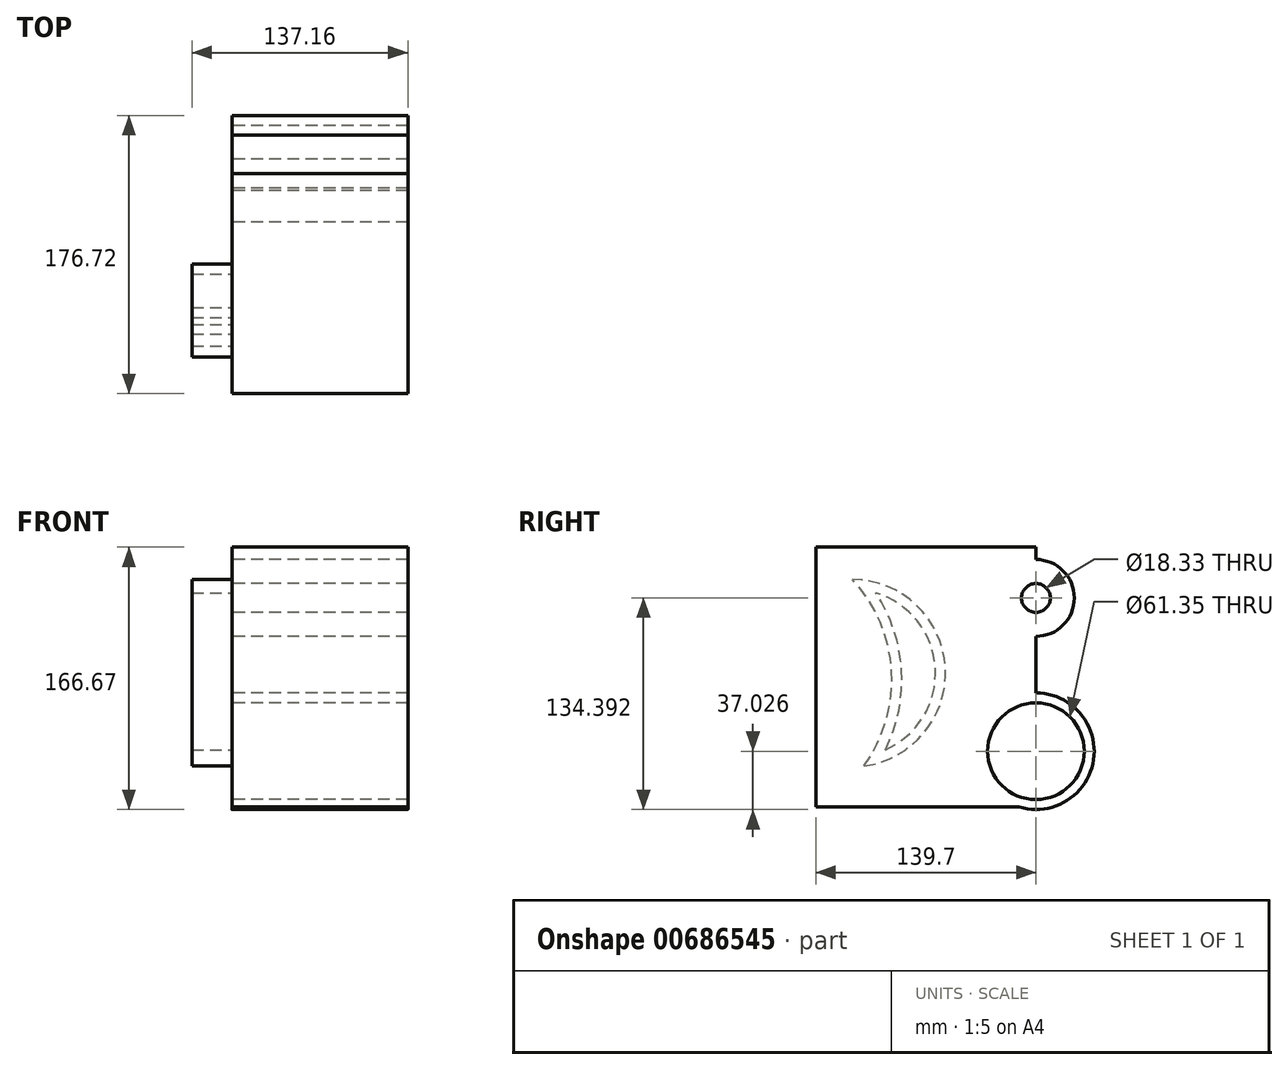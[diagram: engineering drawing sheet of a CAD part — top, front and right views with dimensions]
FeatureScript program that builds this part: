
annotation { "Feature Type Name" : "Feature", "Feature Type Description" : "" }
export const myFeature = defineFeature(function(context is Context, id is Id, definition is map)
    precondition{}
    {
        {
            var Q0;
            Q0=qCreatedBy(makeId("Right.planeOp"),FACE);
            var sketch = newSketch(context, id + "F0", { "sketchPlane" : qUnion([Q0])});
            skCircle(sketch, "E0", {"center": v(69.85, -47.1) * mm, "radius": 37.02 * mm});
            skLineSegment(sketch, "E1.0", {"start": v(-69.85, -82.55) * mm, "end": v(69.85, -82.55) * mm});
            skLineSegment(sketch, "E1.1", {"start": v(-69.85, 82.55) * mm, "end": v(-69.85, -82.55) * mm});
            skLineSegment(sketch, "E1.2", {"start": v(69.85, 82.55) * mm, "end": v(-69.85, 82.55) * mm});
            skLineSegment(sketch, "E1.3", {"start": v(69.85, -82.55) * mm, "end": v(69.85, 82.55) * mm});
            skCircle(sketch, "E2", {"center": v(69.85, 50.27) * mm, "radius": 24.4 * mm});
            skCircle(sketch, "E3.0", {"center": v(69.85, 50.27) * mm, "radius": 9.16 * mm});
            skCircle(sketch, "E4.0", {"center": v(69.85, -47.1) * mm, "radius": 30.67 * mm});
            skSolve(sketch);
        }
        {
            var Q0;
            {var subQ0=sQuery(id+"F0.wireOp",EDGE,"E1.1");Q0=makeQuery(id+"F0.imprint","IMPRINT",FACE,{"disambiguationData":[TD([[makeQuery(id+"F0.imprint","IMPRINT",EDGE,{"derivedFrom":subQ0}),1.0]])]});}
            var Q1;
            {var subQ1=sQuery(id+"F0.wireOp",EDGE,"E0");var subQ6=sQuery(id+"F0.wireOp",EDGE,"E1.0");var subQ8=makeQuery(id+"F0.imprint","INTERSECT",VERTEX,{"derivedFrom":[subQ1,subQ6]});Q1=makeQuery(id+"F0.imprint","IMPRINT",FACE,{"disambiguationData":[TD([[makeQuery(id+"F0.imprint","IMPRINT",EDGE,{"disambiguationData":[TD([[subQ8,-1.0]])],"derivedFrom":subQ1}),1.0]])]});}
            var Q2;
            {var subQ0=sQuery(id+"F0.wireOp",EDGE,"E2");var subQ1=sQuery(id+"F0.wireOp",EDGE,"E1.3");var subQ2=makeQuery(id+"F0.imprint","INTERSECT",VERTEX,{"disambiguationData":[OD(0.0)],"derivedFrom":[subQ1,subQ0]});Q2=makeQuery(id+"F0.imprint","IMPRINT",FACE,{"disambiguationData":[TD([[makeQuery(id+"F0.imprint","IMPRINT",EDGE,{"disambiguationData":[TD([[subQ2,-1.0]])],"derivedFrom":subQ1}),-1.0]])]});}
            var Q3;
            {var subQ1=sQuery(id+"F0.wireOp",EDGE,"E1.0");var subQ5=sQuery(id+"F0.wireOp",EDGE,"E0");var subQ8=makeQuery(id+"F0.imprint","INTERSECT",VERTEX,{"derivedFrom":[subQ5,subQ1]});Q3=makeQuery(id+"F0.imprint","IMPRINT",FACE,{"disambiguationData":[TD([[makeQuery(id+"F0.imprint","IMPRINT",EDGE,{"disambiguationData":[TD([[subQ8,1.0]])],"derivedFrom":subQ5}),1.0]])]});}
            var Q4;
            {var subQ0=sQuery(id+"F0.wireOp",EDGE,"E2");var subQ1=sQuery(id+"F0.wireOp",EDGE,"E1.3");var subQ2=makeQuery(id+"F0.imprint","INTERSECT",VERTEX,{"disambiguationData":[OD(0.0)],"derivedFrom":[subQ1,subQ0]});Q4=makeQuery(id+"F0.imprint","IMPRINT",FACE,{"disambiguationData":[TD([[makeQuery(id+"F0.imprint","IMPRINT",EDGE,{"disambiguationData":[TD([[subQ2,-1.0]])],"derivedFrom":subQ1}),1.0]])]});}
            extrude(context, id + "F1", {"entities" : qUnion([Q0, Q1, Q2, Q3, Q4]), "depth" : 111.76 * mm, "offsetDistance" : 25.4 * mm});
        }
        {
            var Q0;
            Q0=makeQuery(id+"F1.opExtrude","CAP_FACE",FACE,{"disambiguationData":[OSD([sQuery(id+"F0.wireOp",EDGE,"E0"),sQuery(id+"F0.wireOp",EDGE,"E1.0"),sQuery(id+"F0.wireOp",EDGE,"E1.1"),sQuery(id+"F0.wireOp",EDGE,"E1.2"),sQuery(id+"F0.wireOp",EDGE,"E1.3"),sQuery(id+"F0.wireOp",EDGE,"E2"),sQuery(id+"F0.wireOp",EDGE,"E3.0"),sQuery(id+"F0.wireOp",EDGE,"E4.0")])],"isStart":false});
            var sketch = newSketch(context, id + "F2", { "sketchPlane" : qUnion([Q0])});
            skSolve(sketch);
        }
        {
            var Q0;
            Q0=makeQuery(id+"F1.opExtrude","CAP_FACE",FACE,{"disambiguationData":[OSD([sQuery(id+"F0.wireOp",EDGE,"E0"),sQuery(id+"F0.wireOp",EDGE,"E1.0"),sQuery(id+"F0.wireOp",EDGE,"E1.1"),sQuery(id+"F0.wireOp",EDGE,"E1.2"),sQuery(id+"F0.wireOp",EDGE,"E1.3"),sQuery(id+"F0.wireOp",EDGE,"E2"),sQuery(id+"F0.wireOp",EDGE,"E3.0"),sQuery(id+"F0.wireOp",EDGE,"E4.0")])],"isStart":true});
            var sketch = newSketch(context, id + "F3", { "sketchPlane" : qUnion([Q0])});
            skArc(sketch, "E5", {"start": v(31.85, 53.46) * mm, "mid": v(-5.96, 5.73) * mm, "end": v(25.85, -46.2) * mm});
            skArc(sketch, "E6", {"start": v(31.85, 53.46) * mm, "mid": v(15.48, 4.44) * mm, "end": v(25.85, -46.2) * mm});
            skArc(sketch, "E7.0", {"start": v(46.67, 62.05) * mm, "mid": v(-12.3, 6.11) * mm, "end": v(39.52, -56.5) * mm});
            skArc(sketch, "E7.1", {"start": v(46.67, 62.05) * mm, "mid": v(21.82, 4.06) * mm, "end": v(39.52, -56.5) * mm});
            skSolve(sketch);
        }
        {
            var Q0;
            Q0 = qSketchRegion(id + "F3", true);
            extrude(context, id + "F4", {"entities" : qUnion([Q0]), "operationType" : NewBodyOperationType.ADD, "depth" : 25.4 * mm, "offsetDistance" : 25.4 * mm});
        }
    });
